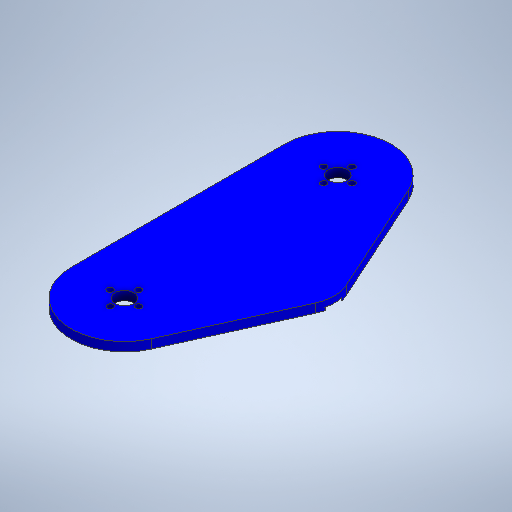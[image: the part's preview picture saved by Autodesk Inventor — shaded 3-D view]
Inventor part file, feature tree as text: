
AUTODESK INVENTOR PART (.ipt)
format: ipt  version: 2025.2 (Build 292293000, 293)  size: 267,264 bytes
history: native  units: mm
features: sketch x2, extrude x2, hole x2
ambient origin geometry x8: Origin, YZ Plane, XZ Plane, XY Plane, X Axis, Y Axis, Z Axis, Center Point
bodies: Solid1 (feature_tree)
feature tree (6):
  sketch  "Sketch1"  dims[d0=120.0mm d1=60.0mm]
  extrude  "Extrusion1"  Depth=60.0mm
  hole  "Hole1"  [1 undecoded]
  extrude  "Extrusion2"  Depth=30.0mm
  hole  "Hole2"  [1 undecoded]
  sketch  "Sketch Circular Pattern1"  dims[d2=120.0mm d3=5.0mm d4=0.0mm d5=21.0mm d6=10.6mm d7=6.0mm d8=4.0mm d9=2.0mm d10=90.0deg d11=8.0mm d12=20.594885mm d13=1.5mm d14=0.0mm d15=8.0mm d16=3.5mm d17=40.0mm d19=360.0deg d21=3.5mm d22=6.0mm d23=4.0mm d24=2.0mm d25=90.0deg d26=8.0mm d27=20.594885mm d28=30.0mm d29=12.0mm]
note: 2 required parameter values undecoded (feature->parameter linkage not recoverable at this tier; creation-order binding heuristic only, values carry confidence <= 0.55)
